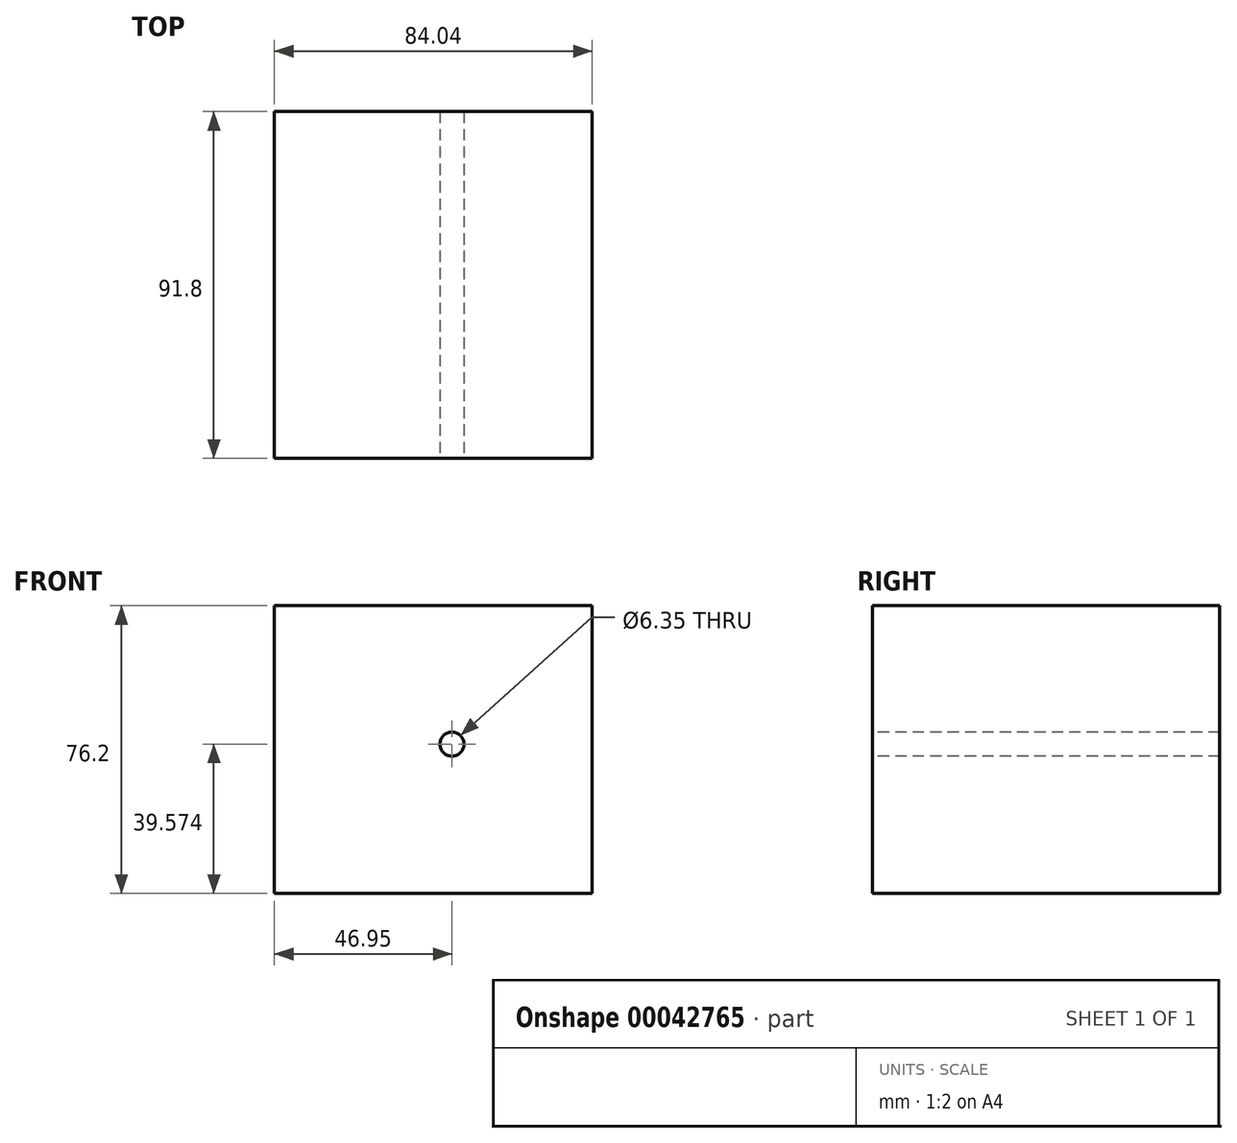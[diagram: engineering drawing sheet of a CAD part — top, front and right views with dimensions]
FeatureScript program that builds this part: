
annotation { "Feature Type Name" : "Feature", "Feature Type Description" : "" }
export const myFeature = defineFeature(function(context is Context, id is Id, definition is map)
    precondition{}
    {
        {
            var Q0;
            Q0=qCreatedBy(makeId("Top.planeOp"),FACE);
            var sketch = newSketch(context, id + "F0", { "sketchPlane" : qUnion([Q0])});
            skLineSegment(sketch, "E0.bottom", {"start": v(-46.95, -46.45) * mm, "end": v(37.1, -46.45) * mm});
            skLineSegment(sketch, "E0.top", {"start": v(-46.95, 45.35) * mm, "end": v(37.1, 45.35) * mm});
            skLineSegment(sketch, "E0.left", {"start": v(-46.95, -46.45) * mm, "end": v(-46.95, 45.35) * mm});
            skLineSegment(sketch, "E0.right", {"start": v(37.1, -46.45) * mm, "end": v(37.1, 45.35) * mm});
            skSolve(sketch);
        }
        {
            var Q0;
            Q0=makeQuery(id+"F0.imprint","IMPRINT",FACE,{"disambiguationData":[TD([[makeQuery(id+"F0.imprint","IMPRINT",EDGE,{"derivedFrom":sQuery(id+"F0.wireOp",EDGE,"E0.bottom")}),1.0]])]});
            extrude(context, id + "F1", {"entities" : qUnion([Q0]), "depth" : 76.2 * mm});
        }
        {
            var Q0;
            Q0=makeQuery(id+"F1.opExtrude","SWEPT_FACE",FACE,{"disambiguationData":[OSD([sQuery(id+"F0.wireOp",EDGE,"E0.bottom")])]});
            var sketch = newSketch(context, id + "F2", { "sketchPlane" : qUnion([Q0])});
            skCircle(sketch, "E1", {"center": v(0, 39.57) * mm, "radius": 20.41 * mm});
            skSolve(sketch);
        }
        {
            var Q0;
            Q0=sQuery(id+"F2.wireOp",VERTEX,"E1.center");
            var Q1;
            Q1=makeQuery(id+"F1.opExtrude","SWEPT_BODY",BODY,{"disambiguationData":[OSD([sQuery(id+"F0.wireOp",EDGE,"E0.bottom"),sQuery(id+"F0.wireOp",EDGE,"E0.top"),sQuery(id+"F0.wireOp",EDGE,"E0.left"),sQuery(id+"F0.wireOp",EDGE,"E0.right")])]});
            hole(context, id + "F3", {"style" : HoleStyle.SIMPLE, "holeDiameter" : 6.35 * mm, "endStyle" : HoleEndStyle.THROUGH, "locations" : qUnion([Q0]), "scope" : qUnion([Q1])});
        }
    });
